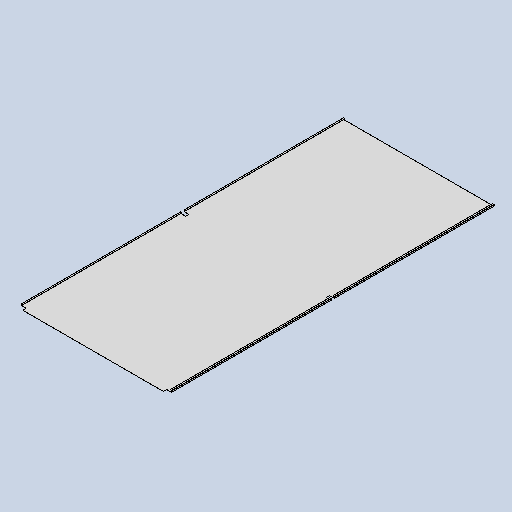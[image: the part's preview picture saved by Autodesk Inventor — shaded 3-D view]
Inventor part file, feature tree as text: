
AUTODESK INVENTOR PART (.ipt)
format: ipt  version: 2025 (Build 290162010, 162A)  size: 288,256 bytes
history: native  units: mm
features: sheet_metal_op x7, sketch x4, other x4, extrude x1, chamfer x1, projected_geometry x1
ambient origin geometry x8: Origin, YZ Plane, XZ Plane, XY Plane, X Axis, Y Axis, Z Axis, Center Point
bodies: Body1 (feature_tree)
feature tree (18):
  sheet_metal_op  "Face1"
  sheet_metal_op  "Flange1"
  sheet_metal_op  "Flange2"
  extrude  "Extrusion3"  Depth=915.0mm
  chamfer  "Corner Round1"
  sketch  "Sketch6"  dims[d12=23.212879mm d52=915.0mm]
  other  "Plate2"
  sketch  "Sketch10"  dims[d53=1980.0mm]
  other  "Plate3"
  sheet_metal_op  "Bend2"
  sheet_metal_op  "Corner2"
  sketch  "Sketch11"  dims[d54=0.5mm]
  other  "Plate4"
  sheet_metal_op  "Bend3"
  sheet_metal_op  "Corner3"
  sketch  "Sketch12"  dims[d74=0.5mm d75=0.25mm d76=1.0mm d77=0.5mm d78=10.0mm d79=90.0deg d80=0.5mm d81=2.0mm d82=0.5mm d83=0.5mm d84=0.5mm d85=0.25mm d86=1.0mm d87=0.5mm d88=10.0mm d89=90.0deg d90=0.5mm d91=2.0mm d92=0.5mm d93=0.5mm d94=0.0mm d95=0.0mm d96=20.0mm d97=30.0mm d109=990.0mm d110=30.0mm d111=4.0mm]
  projected_geometry  "Projected Loop5"
  other  "Definition1"
